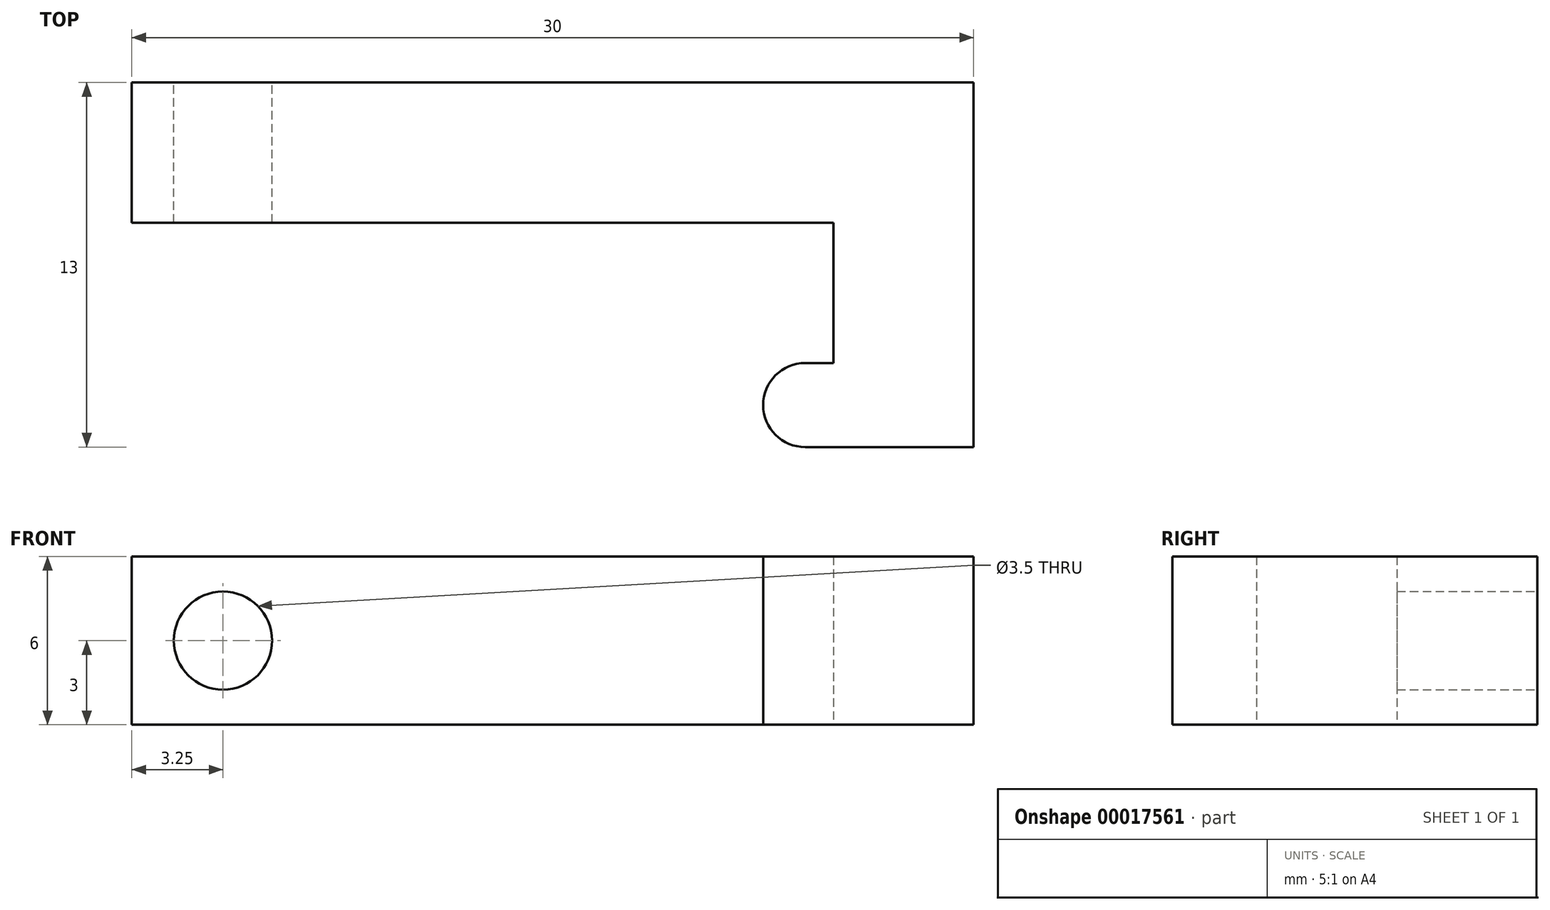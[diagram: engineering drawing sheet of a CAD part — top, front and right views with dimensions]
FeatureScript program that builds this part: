
annotation { "Feature Type Name" : "Feature", "Feature Type Description" : "" }
export const myFeature = defineFeature(function(context is Context, id is Id, definition is map)
    precondition{}
    {
        {
            var Q0;
            Q0=qCreatedBy(makeId("Top.planeOp"),FACE);
            var sketch = newSketch(context, id + "F0", { "sketchPlane" : qUnion([Q0])});
            skLineSegment(sketch, "E0", {"start": v(0, 0) * mm, "end": v(5, 0) * mm});
            skLineSegment(sketch, "E1", {"start": v(5, 0) * mm, "end": v(5, 13) * mm});
            skLineSegment(sketch, "E2", {"start": v(5, 13) * mm, "end": v(-25, 13) * mm});
            skLineSegment(sketch, "E3", {"start": v(-25, 13) * mm, "end": v(-25, 8) * mm});
            skLineSegment(sketch, "E4", {"start": v(-25, 8) * mm, "end": v(0, 8) * mm});
            skLineSegment(sketch, "E5", {"start": v(0, 8) * mm, "end": v(0, 3) * mm});
            skLineSegment(sketch, "E6", {"start": v(0, 3) * mm, "end": v(-1, 3) * mm});
            skLineSegment(sketch, "E7", {"start": v(0, 0) * mm, "end": v(-1, 0) * mm});
            skArc(sketch, "E8", {"start": v(-1, 3) * mm, "mid": v(-2.5, 1.5) * mm, "end": v(-1, 0) * mm});
            skSolve(sketch);
        }
        {
            var Q0;
            Q0=qSketchRegion(id+"F0",true);
            extrude(context, id + "F1", {"entities" : qUnion([Q0]), "depth" : 6 * mm});
        }
        {
            var Q0;
            Q0=makeQuery(id+"F1.opExtrude","SWEPT_FACE",FACE,{"disambiguationData":[OSD([sQuery(id+"F0.wireOp",EDGE,"E2")])]});
            var sketch = newSketch(context, id + "F2", { "sketchPlane" : qUnion([Q0])});
            skCircle(sketch, "E9", {"center": v(21.75, 3) * mm, "radius": 1.75 * mm});
            skLineSegment(sketch, "E10", {"start": v(21.75, 6) * mm, "end": v(21.75, 0) * mm});
            skSolve(sketch);
        }
        {
            var Q0;
            Q0=qSketchRegion(id+"F2",true);
            extrude(context, id + "F3", {"entities" : qUnion([Q0]), "operationType" : NewBodyOperationType.REMOVE, "oppositeDirection" : true, "depth" : 25 * mm});
        }
    });
